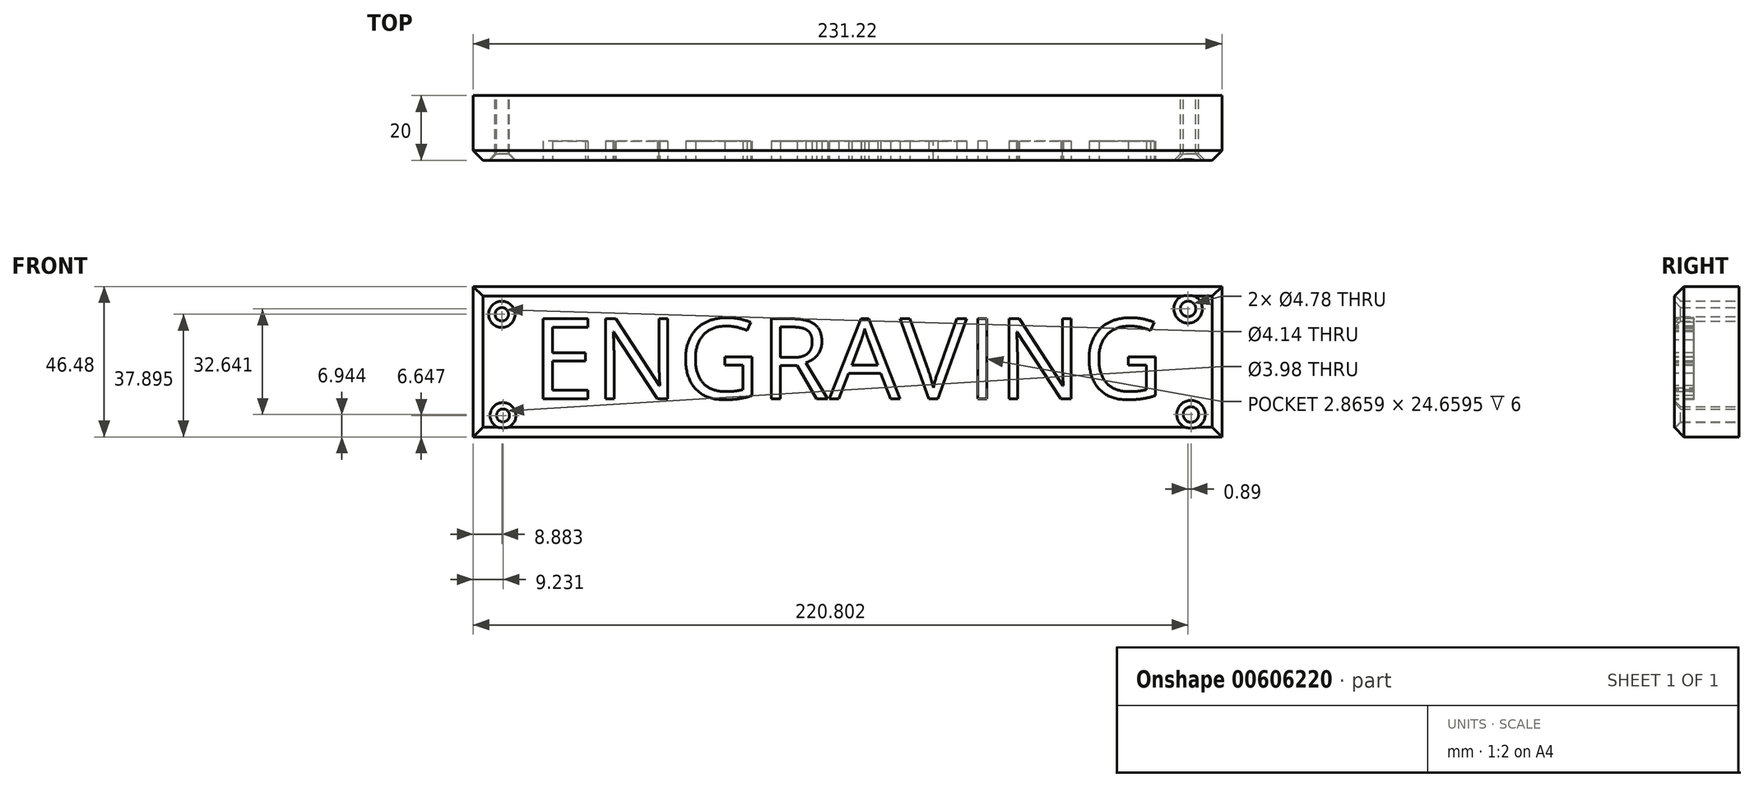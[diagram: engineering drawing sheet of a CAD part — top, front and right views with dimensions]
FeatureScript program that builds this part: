
annotation { "Feature Type Name" : "Feature", "Feature Type Description" : "" }
export const myFeature = defineFeature(function(context is Context, id is Id, definition is map)
    precondition{}
    {
        {
            var Q0;
            Q0=qCreatedBy(makeId("Front.planeOp"),FACE);
            var sketch = newSketch(context, id + "F0", { "sketchPlane" : qUnion([Q0])});
            skLineSegment(sketch, "E0.bottom", {"start": v(115.6, -23.24) * mm, "end": v(-115.6, -23.24) * mm});
            skLineSegment(sketch, "E0.top", {"start": v(115.6, 23.24) * mm, "end": v(-115.6, 23.24) * mm});
            skLineSegment(sketch, "E0.left", {"start": v(115.6, -23.24) * mm, "end": v(115.6, 23.24) * mm});
            skLineSegment(sketch, "E0.right", {"start": v(-115.6, -23.24) * mm, "end": v(-115.6, 23.24) * mm});
            skPoint(sketch, "E0.middle", {"position": v(0, 0) * mm});
            skSolve(sketch);
        }
        {
            var Q0;
            Q0 = qSketchRegion(id + "F0", true);
            extrude(context, id + "F1", {"entities" : qUnion([Q0]), "depth" : 20 * mm, "offsetDistance" : 25 * mm});
        }
        {
            var Q0;
            Q0=qCreatedBy(makeId("Front.planeOp"),FACE);
            cPlane(context, id + "F2", {"entities" : qUnion([Q0]), "cplaneType" : CPlaneType.OFFSET, "offset" : 20 * mm, "width" : 150 * mm, "height" : 150 * mm});
        }
        {
            var Q0;
            Q0=qCreatedBy(id+"F2.planeOp",FACE);
            var sketch = newSketch(context, id + "F3", { "sketchPlane" : qUnion([Q0])});
            skText(sketch, "E1", { "text": "ENGRAVING", "fontName": "OpenSans-Regular.ttf"});
            const initialGuessF3  = {"E1": [-0.09734, -0.0114, 1, 0, 0.02487]};
            skSetInitialGuess(sketch, initialGuessF3);
            skSolve(sketch);
        }
        {
            var Q0;
            Q0 = qSketchRegion(id + "F3", true);
            extrude(context, id + "F4", {"entities" : qUnion([Q0]), "operationType" : NewBodyOperationType.REMOVE, "oppositeDirection" : true, "depth" : 6 * mm, "offsetDistance" : 25 * mm});
        }
        {
            var Q0;
            Q0=qCreatedBy(id+"F2.planeOp",FACE);
            var sketch = newSketch(context, id + "F5", { "sketchPlane" : qUnion([Q0])});
            skPoint(sketch, "E2", {"position": v(-105.84, 15.54) * mm});
            skCircle(sketch, "E3", {"center": v(-105.84, 15.54) * mm, "radius": 2.65 * mm});
            skSolve(sketch);
        }
        {
            var Q0;
            Q0 = qSketchRegion(id + "F5", true);
            extrude(context, id + "F6", {"entities" : qUnion([Q0]), "operationType" : NewBodyOperationType.REMOVE, "depth" : 25 * mm, "offsetDistance" : 25 * mm});
        }
        {
            var Q0;
            Q0=qCreatedBy(makeId("Front.planeOp"),FACE);
            var sketch = newSketch(context, id + "F7", { "sketchPlane" : qUnion([Q0])});
            skPoint(sketch, "E4", {"position": v(-106.73, 14.65) * mm});
            skCircle(sketch, "E5", {"center": v(-106.73, 14.65) * mm, "radius": 2.07 * mm});
            skSolve(sketch);
        }
        {
            var Q0;
            Q0 = qSketchRegion(id + "F7", true);
            extrude(context, id + "F8", {"entities" : qUnion([Q0]), "operationType" : NewBodyOperationType.REMOVE, "depth" : 25 * mm, "offsetDistance" : 25 * mm});
        }
        {
            var Q0;
            Q0=qCreatedBy(makeId("Front.planeOp"),FACE);
            var sketch = newSketch(context, id + "F9", { "sketchPlane" : qUnion([Q0])});
            skCircle(sketch, "E6", {"center": v(-106.38, -16.6) * mm, "radius": 2 * mm});
            skSolve(sketch);
        }
        {
            var Q0;
            Q0 = qSketchRegion(id + "F9", true);
            extrude(context, id + "F10", {"entities" : qUnion([Q0]), "operationType" : NewBodyOperationType.REMOVE, "depth" : 25 * mm, "offsetDistance" : 25 * mm});
        }
        {
            var Q0;
            Q0=qCreatedBy(makeId("Front.planeOp"),FACE);
            var sketch = newSketch(context, id + "F11", { "sketchPlane" : qUnion([Q0])});
            skCircle(sketch, "E7", {"center": v(105.2, 16.34) * mm, "radius": 2.4 * mm});
            skSolve(sketch);
        }
        {
            var Q0;
            Q0 = qSketchRegion(id + "F11", true);
            extrude(context, id + "F12", {"entities" : qUnion([Q0]), "operationType" : NewBodyOperationType.REMOVE, "depth" : 25 * mm, "offsetDistance" : 25 * mm});
        }
        {
            var Q0;
            Q0=qCreatedBy(makeId("Front.planeOp"),FACE);
            var sketch = newSketch(context, id + "F13", { "sketchPlane" : qUnion([Q0])});
            skCircle(sketch, "E8", {"center": v(106.08, -16.3) * mm, "radius": 2.4 * mm});
            skSolve(sketch);
        }
        {
            var Q0;
            Q0 = qSketchRegion(id + "F13", true);
            extrude(context, id + "F14", {"entities" : qUnion([Q0]), "operationType" : NewBodyOperationType.REMOVE, "depth" : 25 * mm, "offsetDistance" : 25 * mm});
        }
        {
            var Q0;
            {var subQ0=sQuery(id+"F0.wireOp",EDGE,"E0.left");var subQ1=sQuery(id+"F0.wireOp",EDGE,"E0.top");var subQ2=sQuery(id+"F0.wireOp",EDGE,"E0.right");var subQ3=sQuery(id+"F0.wireOp",EDGE,"E0.bottom");Q0=makeQuery(id+"F8.boolean.opBoolean","INTERSECT",EDGE,{"derivedFrom":[makeQuery(id+"F4.boolean.opBoolean","SPLIT",FACE,{"disambiguationData":[TD([makeQuery(id+"F1.opExtrude","SWEPT_FACE",FACE,{"disambiguationData":[OSD([subQ3])]})])],"derivedFrom":makeQuery(id+"F1.opExtrude","CAP_FACE",FACE,{"disambiguationData":[OSD([subQ3,subQ1,subQ0,subQ2])],"isStart":false})}),makeQuery(id+"F8.opExtrude","SWEPT_FACE",FACE,{"disambiguationData":[OSD([sQuery(id+"F7.wireOp",EDGE,"E5")])]})]});}
            chamfer(context, id + "F15", {"entities" : qUnion([Q0]), "width" : 2 * mm, "tangentPropagation" : true});
        }
        {
            var Q0;
            {var subQ0=sQuery(id+"F0.wireOp",EDGE,"E0.left");var subQ1=sQuery(id+"F0.wireOp",EDGE,"E0.top");var subQ2=sQuery(id+"F0.wireOp",EDGE,"E0.right");var subQ3=sQuery(id+"F0.wireOp",EDGE,"E0.bottom");Q0=makeQuery(id+"F10.boolean.opBoolean","INTERSECT",EDGE,{"derivedFrom":[makeQuery(id+"F4.boolean.opBoolean","SPLIT",FACE,{"disambiguationData":[TD([makeQuery(id+"F1.opExtrude","SWEPT_FACE",FACE,{"disambiguationData":[OSD([subQ3])]})])],"derivedFrom":makeQuery(id+"F1.opExtrude","CAP_FACE",FACE,{"disambiguationData":[OSD([subQ3,subQ1,subQ0,subQ2])],"isStart":false})}),makeQuery(id+"F10.opExtrude","SWEPT_FACE",FACE,{"disambiguationData":[OSD([sQuery(id+"F9.wireOp",EDGE,"E6")])]})]});}
            chamfer(context, id + "F16", {"entities" : qUnion([Q0]), "width" : 2 * mm, "tangentPropagation" : true});
        }
        {
            var Q0;
            {var subQ0=sQuery(id+"F0.wireOp",EDGE,"E0.left");var subQ1=sQuery(id+"F0.wireOp",EDGE,"E0.top");var subQ2=sQuery(id+"F0.wireOp",EDGE,"E0.right");var subQ3=sQuery(id+"F0.wireOp",EDGE,"E0.bottom");Q0=makeQuery(id+"F12.boolean.opBoolean","INTERSECT",EDGE,{"derivedFrom":[makeQuery(id+"F4.boolean.opBoolean","SPLIT",FACE,{"disambiguationData":[TD([makeQuery(id+"F1.opExtrude","SWEPT_FACE",FACE,{"disambiguationData":[OSD([subQ3])]})])],"derivedFrom":makeQuery(id+"F1.opExtrude","CAP_FACE",FACE,{"disambiguationData":[OSD([subQ3,subQ1,subQ0,subQ2])],"isStart":false})}),makeQuery(id+"F12.opExtrude","SWEPT_FACE",FACE,{"disambiguationData":[OSD([sQuery(id+"F11.wireOp",EDGE,"E7")])]})]});}
            chamfer(context, id + "F17", {"entities" : qUnion([Q0]), "width" : 2 * mm, "tangentPropagation" : true});
        }
        {
            var Q0;
            {var subQ0=sQuery(id+"F0.wireOp",EDGE,"E0.left");var subQ1=sQuery(id+"F0.wireOp",EDGE,"E0.top");var subQ2=sQuery(id+"F0.wireOp",EDGE,"E0.right");var subQ3=sQuery(id+"F0.wireOp",EDGE,"E0.bottom");Q0=makeQuery(id+"F14.boolean.opBoolean","INTERSECT",EDGE,{"derivedFrom":[makeQuery(id+"F4.boolean.opBoolean","SPLIT",FACE,{"disambiguationData":[TD([makeQuery(id+"F1.opExtrude","SWEPT_FACE",FACE,{"disambiguationData":[OSD([subQ3])]})])],"derivedFrom":makeQuery(id+"F1.opExtrude","CAP_FACE",FACE,{"disambiguationData":[OSD([subQ3,subQ1,subQ0,subQ2])],"isStart":false})}),makeQuery(id+"F14.opExtrude","SWEPT_FACE",FACE,{"disambiguationData":[OSD([sQuery(id+"F13.wireOp",EDGE,"E8")])]})]});}
            chamfer(context, id + "F18", {"entities" : qUnion([Q0]), "width" : 2 * mm, "tangentPropagation" : true});
        }
        {
            var Q0;
            Q0=makeQuery(id+"F1.opExtrude","CAP_EDGE",EDGE,{"disambiguationData":[OSD([sQuery(id+"F0.wireOp",EDGE,"E0.top")])],"isStart":false});
            var Q1;
            Q1=makeQuery(id+"F1.opExtrude","CAP_EDGE",EDGE,{"disambiguationData":[OSD([sQuery(id+"F0.wireOp",EDGE,"E0.right")])],"isStart":false});
            var Q2;
            Q2=makeQuery(id+"F1.opExtrude","CAP_EDGE",EDGE,{"disambiguationData":[OSD([sQuery(id+"F0.wireOp",EDGE,"E0.bottom")])],"isStart":false});
            var Q3;
            Q3=makeQuery(id+"F1.opExtrude","CAP_EDGE",EDGE,{"disambiguationData":[OSD([sQuery(id+"F0.wireOp",EDGE,"E0.left")])],"isStart":false});
            chamfer(context, id + "F19", {"entities" : qUnion([Q0, Q1, Q2, Q3]), "width" : 3 * mm, "tangentPropagation" : true});
        }
    });
